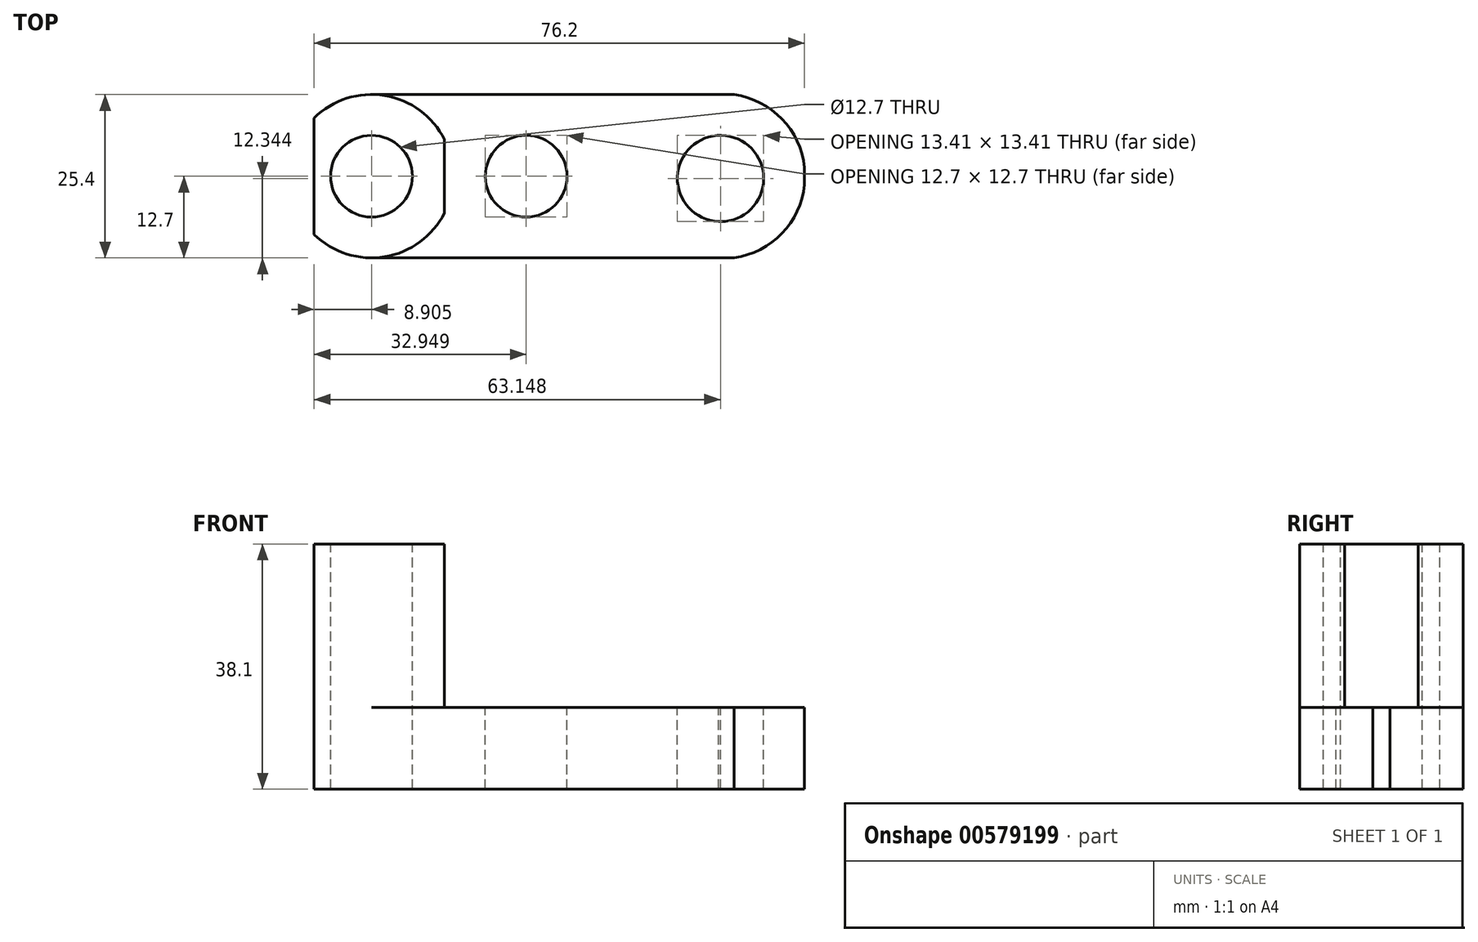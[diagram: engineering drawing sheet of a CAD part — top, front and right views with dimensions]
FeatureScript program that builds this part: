
annotation { "Feature Type Name" : "Feature", "Feature Type Description" : "" }
export const myFeature = defineFeature(function(context is Context, id is Id, definition is map)
    precondition{}
    {
        {
            var Q0;
            Q0=qCreatedBy(makeId("Front.planeOp"),FACE);
            var sketch = newSketch(context, id + "F0", { "sketchPlane" : qUnion([Q0])});
            skLineSegment(sketch, "E0", {"start": v(-61.64, 38.1) * mm, "end": v(-61.64, 0) * mm});
            skLineSegment(sketch, "E1", {"start": v(-61.64, 0) * mm, "end": v(14.56, 0) * mm});
            skLineSegment(sketch, "E2", {"start": v(14.56, 0) * mm, "end": v(14.56, 12.7) * mm});
            skLineSegment(sketch, "E3", {"start": v(14.56, 12.7) * mm, "end": v(-41.4, 12.7) * mm});
            skLineSegment(sketch, "E4", {"start": v(-41.4, 12.7) * mm, "end": v(-41.4, 38.1) * mm});
            skLineSegment(sketch, "E5", {"start": v(-41.4, 38.1) * mm, "end": v(-61.64, 38.1) * mm});
            skSolve(sketch);
        }
        {
            var Q0;
            Q0=makeQuery(id+"F0.imprint","IMPRINT",FACE,{"disambiguationData":[TD([[makeQuery(id+"F0.imprint","IMPRINT",EDGE,{"derivedFrom":sQuery(id+"F0.wireOp",EDGE,"E0")}),1.0]])]});
            extrude(context, id + "F1", {"entities" : qUnion([Q0]), "depth" : 25.4 * mm, "offsetDistance" : 25.4 * mm});
        }
        {
            var Q0;
            Q0=makeQuery(id+"F1.opExtrude","SWEPT_FACE",FACE,{"disambiguationData":[OSD([sQuery(id+"F0.wireOp",EDGE,"E3")])]});
            var sketch = newSketch(context, id + "F2", { "sketchPlane" : qUnion([Q0])});
            skCircle(sketch, "E6", {"center": v(-28.7, -12.7) * mm, "radius": 6.35 * mm});
            skCircle(sketch, "E7", {"center": v(1.5, -13.06) * mm, "radius": 6.7 * mm});
            skLineSegment(sketch, "E8", {"start": v(-28.74, -6.35) * mm, "end": v(1.5, -6.35) * mm});
            skLineSegment(sketch, "E9", {"start": v(1.5, -6.35) * mm, "end": v(1.5, -19.76) * mm});
            skLineSegment(sketch, "E10", {"start": v(1.5, -19.76) * mm, "end": v(-28.84, -19.05) * mm});
            skSolve(sketch);
        }
        {
            var Q0;
            {var subQ0=sQuery(id+"F2.wireOp",EDGE,"E6");var subQ2=makeQuery(id+"F2.imprint","IMPRINT",VERTEX,{"derivedFrom":subQ0});Q0=makeQuery(id+"F2.imprint","IMPRINT",FACE,{"disambiguationData":[TD([[makeQuery(id+"F2.imprint","IMPRINT",EDGE,{"disambiguationData":[TD([[subQ2,1.0]])],"derivedFrom":subQ0}),1.0]])]});}
            var Q1;
            {var subQ0=sQuery(id+"F2.wireOp",EDGE,"E8");Q1=makeQuery(id+"F2.imprint","IMPRINT",FACE,{"disambiguationData":[TD([[makeQuery(id+"F2.imprint","IMPRINT",EDGE,{"derivedFrom":subQ0}),-1.0]])]});}
            var Q2;
            {var subQ0=sQuery(id+"F2.wireOp",EDGE,"E9");Q2=makeQuery(id+"F2.imprint","IMPRINT",FACE,{"disambiguationData":[TD([[makeQuery(id+"F2.imprint","IMPRINT",EDGE,{"derivedFrom":subQ0}),-1.0]])]});}
            var Q3;
            {var subQ0=sQuery(id+"F2.wireOp",EDGE,"E9");Q3=makeQuery(id+"F2.imprint","IMPRINT",FACE,{"disambiguationData":[TD([[makeQuery(id+"F2.imprint","IMPRINT",EDGE,{"derivedFrom":subQ0}),1.0]])]});}
            extrude(context, id + "F3", {"entities" : qUnion([Q0, Q1, Q2, Q3]), "operationType" : NewBodyOperationType.REMOVE, "endBound" : BoundingType.THROUGH_ALL, "oppositeDirection" : true, "depth" : 25.4 * mm, "offsetDistance" : 25.4 * mm});
        }
        {
            var Q0;
            Q0=makeQuery(id+"F1.opExtrude","SWEPT_FACE",FACE,{"disambiguationData":[OSD([sQuery(id+"F0.wireOp",EDGE,"E3")])]});
            var sketch = newSketch(context, id + "F4", { "sketchPlane" : qUnion([Q0])});
            skArc(sketch, "E11", {"start": v(0, -25.4) * mm, "mid": v(14.63, -12.7) * mm, "end": v(0, 0) * mm});
            skSolve(sketch);
        }
        {
            var Q0;
            {var subQ0=sQuery(id+"F4.wireOp",EDGE,"E11");var subQ1=sQuery(id+"F0.wireOp",EDGE,"E3");var subQ4=makeQuery(id+"F1.opExtrude","CAP_EDGE",EDGE,{"disambiguationData":[OSD([subQ1])],"isStart":true});var subQ5=makeQuery(id+"F4.imprint","INTERSECT",VERTEX,{"disambiguationData":[OD(1.0)],"derivedFrom":[subQ4,subQ0]});Q0=makeQuery(id+"F4.imprint","IMPRINT",FACE,{"disambiguationData":[TD([[makeQuery(id+"F4.imprint","IMPRINT",EDGE,{"disambiguationData":[TD([[subQ5,1.0]])],"derivedFrom":subQ0}),-1.0]])]});}
            var Q1;
            {var subQ0=sQuery(id+"F4.wireOp",EDGE,"E11");var subQ1=sQuery(id+"F0.wireOp",EDGE,"E3");var subQ2=makeQuery(id+"F1.opExtrude","CAP_EDGE",EDGE,{"disambiguationData":[OSD([subQ1])],"isStart":false});var subQ3=makeQuery(id+"F4.imprint","INTERSECT",VERTEX,{"disambiguationData":[OD(1.0)],"derivedFrom":[subQ2,subQ0]});Q1=makeQuery(id+"F4.imprint","IMPRINT",FACE,{"disambiguationData":[TD([[makeQuery(id+"F4.imprint","IMPRINT",EDGE,{"disambiguationData":[TD([[subQ3,-1.0]])],"derivedFrom":subQ0}),-1.0]])]});}
            extrude(context, id + "F5", {"entities" : qUnion([Q0, Q1]), "operationType" : NewBodyOperationType.REMOVE, "endBound" : BoundingType.THROUGH_ALL, "oppositeDirection" : true, "depth" : 25.4 * mm, "offsetDistance" : 25.4 * mm});
        }
        {
            var Q0;
            Q0=makeQuery(id+"F1.opExtrude","SWEPT_FACE",FACE,{"disambiguationData":[OSD([sQuery(id+"F0.wireOp",EDGE,"E5")])]});
            var sketch = newSketch(context, id + "F6", { "sketchPlane" : qUnion([Q0])});
            skCircle(sketch, "E12", {"center": v(-52.73, -12.7) * mm, "radius": 6.35 * mm});
            skPoint(sketch, "E12.centerSnap0", {"position": v(-61.64, -12.7) * mm});
            skCircle(sketch, "E13", {"center": v(-52.73, -12.7) * mm, "radius": 12.7 * mm});
            skSolve(sketch);
        }
        {
            var Q0;
            Q0=makeQuery(id+"F6.imprint","IMPRINT",FACE,{"disambiguationData":[TD([[makeQuery(id+"F6.imprint","IMPRINT",EDGE,{"derivedFrom":sQuery(id+"F6.wireOp",EDGE,"E12")}),1.0]])]});
            var Q1;
            {var subQ0=sQuery(id+"F6.wireOp",EDGE,"E13");var subQ1=sQuery(id+"F0.wireOp",EDGE,"E5");var subQ2=makeQuery(id+"F1.opExtrude","CAP_EDGE",EDGE,{"disambiguationData":[OSD([subQ1])],"isStart":true});var subQ3=makeQuery(id+"F6.imprint","INTERSECT",VERTEX,{"derivedFrom":[subQ2,subQ0]});Q1=makeQuery(id+"F6.imprint","IMPRINT",FACE,{"disambiguationData":[TD([[makeQuery(id+"F6.imprint","IMPRINT",EDGE,{"disambiguationData":[TD([[subQ3,-1.0]])],"derivedFrom":subQ0}),-1.0]])]});}
            var Q2;
            {var subQ0=sQuery(id+"F6.wireOp",EDGE,"E13");var subQ1=sQuery(id+"F0.wireOp",EDGE,"E5");var subQ4=makeQuery(id+"F1.opExtrude","CAP_EDGE",EDGE,{"disambiguationData":[OSD([subQ1])],"isStart":false});var subQ5=makeQuery(id+"F6.imprint","INTERSECT",VERTEX,{"derivedFrom":[subQ4,subQ0]});Q2=makeQuery(id+"F6.imprint","IMPRINT",FACE,{"disambiguationData":[TD([[makeQuery(id+"F6.imprint","IMPRINT",EDGE,{"disambiguationData":[TD([[subQ5,1.0]])],"derivedFrom":subQ0}),-1.0]])]});}
            var Q3;
            {var subQ0=sQuery(id+"F6.wireOp",EDGE,"E13");var subQ1=sQuery(id+"F0.wireOp",EDGE,"E5");var subQ2=makeQuery(id+"F1.opExtrude","CAP_EDGE",EDGE,{"disambiguationData":[OSD([subQ1])],"isStart":true});var subQ3=makeQuery(id+"F6.imprint","INTERSECT",VERTEX,{"derivedFrom":[subQ2,subQ0]});Q3=makeQuery(id+"F6.imprint","IMPRINT",FACE,{"disambiguationData":[TD([[makeQuery(id+"F6.imprint","IMPRINT",EDGE,{"disambiguationData":[TD([[subQ3,1.0]])],"derivedFrom":subQ0}),-1.0]])]});}
            var Q4;
            {var subQ0=sQuery(id+"F6.wireOp",EDGE,"E13");var subQ1=sQuery(id+"F0.wireOp",EDGE,"E5");var subQ2=makeQuery(id+"F1.opExtrude","CAP_EDGE",EDGE,{"disambiguationData":[OSD([subQ1])],"isStart":false});var subQ3=makeQuery(id+"F6.imprint","INTERSECT",VERTEX,{"derivedFrom":[subQ2,subQ0]});Q4=makeQuery(id+"F6.imprint","IMPRINT",FACE,{"disambiguationData":[TD([[makeQuery(id+"F6.imprint","IMPRINT",EDGE,{"disambiguationData":[TD([[subQ3,-1.0]])],"derivedFrom":subQ0}),-1.0]])]});}
            extrude(context, id + "F7", {"entities" : qUnion([Q0, Q1, Q2, Q3, Q4]), "operationType" : NewBodyOperationType.REMOVE, "oppositeDirection" : true, "depth" : 25.4 * mm, "offsetDistance" : 25.4 * mm});
        }
        {
            var Q0;
            {var subQ0=sQuery(id+"F0.wireOp",EDGE,"E5");var subQ1=makeQuery(id+"F1.opExtrude","CAP_EDGE",EDGE,{"disambiguationData":[OSD([subQ0])],"isStart":false});var subQ2=sQuery(id+"F0.wireOp",EDGE,"E0");var subQ3=makeQuery(id+"F1.opExtrude","SWEPT_EDGE",EDGE,{"disambiguationData":[OSD([subQ2,subQ0])]});var subQ4=makeQuery(id+"F6.imprint","INTERSECT",VERTEX,{"derivedFrom":[subQ3,subQ1]});var subQ5=sQuery(id+"F6.wireOp",EDGE,"E13");var subQ6=makeQuery(id+"F6.imprint","INTERSECT",VERTEX,{"derivedFrom":[subQ1,subQ5]});Q0=makeQuery(id+"F7.boolean.opBoolean","COPY",FACE,{"derivedFrom":makeQuery(id+"F7.opExtrude","CAP_FACE",FACE,{"disambiguationData":[OSD([subQ2,subQ0,subQ5]),TDD([makeQuery(id+"F6.imprint","IMPRINT",EDGE,{"disambiguationData":[TD([[subQ6,1.0]])],"derivedFrom":subQ5}),makeQuery(id+"F6.imprint","IMPRINT",EDGE,{"disambiguationData":[TD([[subQ4,-1.0]])],"derivedFrom":subQ3}),makeQuery(id+"F6.imprint","IMPRINT",EDGE,{"disambiguationData":[TD([[subQ6,-1.0]])],"derivedFrom":subQ1})])],"isStart":false})});}
            var Q1;
            {var subQ0=sQuery(id+"F0.wireOp",EDGE,"E5");var subQ1=makeQuery(id+"F1.opExtrude","CAP_EDGE",EDGE,{"disambiguationData":[OSD([subQ0])],"isStart":true});var subQ2=sQuery(id+"F0.wireOp",EDGE,"E0");var subQ3=makeQuery(id+"F1.opExtrude","SWEPT_EDGE",EDGE,{"disambiguationData":[OSD([subQ2,subQ0])]});var subQ4=makeQuery(id+"F6.imprint","INTERSECT",VERTEX,{"derivedFrom":[subQ3,subQ1]});var subQ5=sQuery(id+"F6.wireOp",EDGE,"E13");var subQ6=makeQuery(id+"F6.imprint","INTERSECT",VERTEX,{"derivedFrom":[subQ1,subQ5]});Q1=makeQuery(id+"F7.boolean.opBoolean","COPY",FACE,{"derivedFrom":makeQuery(id+"F7.opExtrude","CAP_FACE",FACE,{"disambiguationData":[OSD([subQ2,subQ0,subQ5]),TDD([makeQuery(id+"F6.imprint","IMPRINT",EDGE,{"disambiguationData":[TD([[subQ6,-1.0]])],"derivedFrom":subQ5}),makeQuery(id+"F6.imprint","IMPRINT",EDGE,{"disambiguationData":[TD([[subQ4,1.0]])],"derivedFrom":subQ3}),makeQuery(id+"F6.imprint","IMPRINT",EDGE,{"disambiguationData":[TD([[subQ6,-1.0]])],"derivedFrom":subQ1})])],"isStart":false})});}
            extrude(context, id + "F8", {"entities" : qUnion([Q0, Q1]), "operationType" : NewBodyOperationType.REMOVE, "oppositeDirection" : true, "depth" : 25.4 * mm, "offsetDistance" : 25.4 * mm});
        }
        {
            var Q0;
            Q0=makeQuery(id+"F7.boolean.opBoolean","COPY",FACE,{"derivedFrom":makeQuery(id+"F7.opExtrude","CAP_FACE",FACE,{"disambiguationData":[OSD([sQuery(id+"F6.wireOp",EDGE,"E12")])],"isStart":false})});
            extrude(context, id + "F9", {"entities" : qUnion([Q0]), "operationType" : NewBodyOperationType.REMOVE, "oppositeDirection" : true, "depth" : 25.4 * mm, "offsetDistance" : 25.4 * mm});
        }
    });
